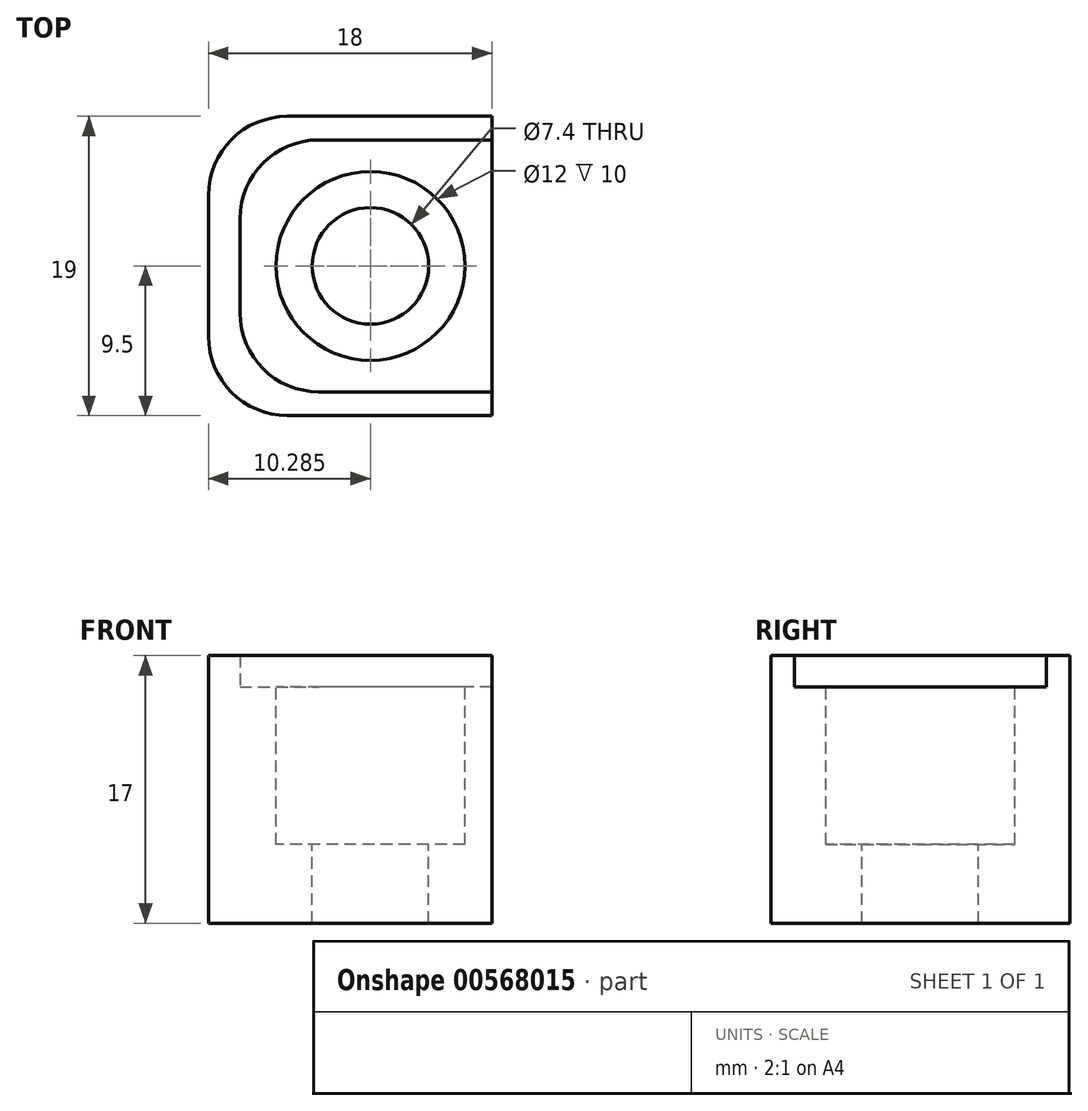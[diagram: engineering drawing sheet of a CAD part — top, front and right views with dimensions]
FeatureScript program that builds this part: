
annotation { "Feature Type Name" : "Feature", "Feature Type Description" : "" }
export const myFeature = defineFeature(function(context is Context, id is Id, definition is map)
    precondition{}
    {
        {
            var Q0;
            Q0=qCreatedBy(makeId("Top.planeOp"),FACE);
            var sketch = newSketch(context, id + "F0", { "sketchPlane" : qUnion([Q0])});
            skLineSegment(sketch, "E0.bottom", {"start": v(8, -8) * mm, "end": v(-8, -8) * mm});
            skLineSegment(sketch, "E0.top", {"start": v(8, 8) * mm, "end": v(-8, 8) * mm});
            skLineSegment(sketch, "E0.left", {"start": v(8, -8) * mm, "end": v(8, 8) * mm});
            skLineSegment(sketch, "E0.right", {"start": v(-8, -8) * mm, "end": v(-8, 8) * mm});
            skPoint(sketch, "E0.middle", {"position": v(0, 0) * mm});
            skLineSegment(sketch, "E1.bottom", {"start": v(8, -9.5) * mm, "end": v(-10, -9.5) * mm});
            skLineSegment(sketch, "E1.top", {"start": v(8, 9.5) * mm, "end": v(-10, 9.5) * mm});
            skLineSegment(sketch, "E1.right", {"start": v(-10, -9.5) * mm, "end": v(-10, 9.5) * mm});
            skLineSegment(sketch, "E2", {"start": v(8, 8) * mm, "end": v(8, 9.5) * mm});
            skLineSegment(sketch, "E3", {"start": v(8, -8) * mm, "end": v(8, -9.5) * mm});
            skPoint(sketch, "E1.left.end.orphan", {"position": v(10, 9.5) * mm});
            skPoint(sketch, "E4.orphan", {"position": v(10, -9.5) * mm});
            skCircle(sketch, "E5", {"center": v(0.29, 0) * mm, "radius": 6 * mm});
            skCircle(sketch, "E6", {"center": v(0.29, 0) * mm, "radius": 3.7 * mm});
            skSolve(sketch);
        }
        {
            var Q0;
            Q0=makeQuery(id+"F0.imprint","IMPRINT",FACE,{"disambiguationData":[TD([[makeQuery(id+"F0.imprint","IMPRINT",EDGE,{"derivedFrom":sQuery(id+"F0.wireOp",EDGE,"E0.bottom")}),-1.0]])]});
            var Q1;
            Q1=makeQuery(id+"F0.imprint","IMPRINT",FACE,{"disambiguationData":[TD([[makeQuery(id+"F0.imprint","IMPRINT",EDGE,{"derivedFrom":sQuery(id+"F0.wireOp",EDGE,"E5")}),1.0]])]});
            extrude(context, id + "F1", {"entities" : qUnion([Q0, Q1]), "oppositeDirection" : true, "depth" : 15 * mm, "offsetDistance" : 25 * mm});
        }
        {
            var Q0;
            Q0=makeQuery(id+"F0.imprint","IMPRINT",FACE,{"disambiguationData":[TD([[makeQuery(id+"F0.imprint","IMPRINT",EDGE,{"derivedFrom":sQuery(id+"F0.wireOp",EDGE,"E0.bottom")}),1.0]])]});
            extrude(context, id + "F2", {"entities" : qUnion([Q0]), "operationType" : NewBodyOperationType.ADD, "depth" : 2 * mm, "offsetDistance" : 25 * mm, "hasSecondDirection" : true, "secondDirectionOppositeDirection" : true, "secondDirectionDepth" : 15 * mm});
        }
        {
            var Q0;
            Q0=makeQuery(id+"F2.opExtrude","SWEPT_EDGE",EDGE,{"disambiguationData":[OSD([sQuery(id+"F0.wireOp",EDGE,"E0.top"),sQuery(id+"F0.wireOp",EDGE,"E0.right")])]});
            var Q1;
            Q1=makeQuery(id+"F2.opExtrude","SWEPT_EDGE",EDGE,{"disambiguationData":[OSD([sQuery(id+"F0.wireOp",EDGE,"E0.bottom"),sQuery(id+"F0.wireOp",EDGE,"E0.right")])]});
            var Q2;
            Q2=makeQuery(id+"F2.opExtrude","SWEPT_EDGE",EDGE,{"disambiguationData":[OSD([sQuery(id+"F0.wireOp",EDGE,"E1.top"),sQuery(id+"F0.wireOp",EDGE,"E1.right")])]});
            var Q3;
            Q3=makeQuery(id+"F2.opExtrude","SWEPT_EDGE",EDGE,{"disambiguationData":[OSD([sQuery(id+"F0.wireOp",EDGE,"E1.bottom"),sQuery(id+"F0.wireOp",EDGE,"E1.right")])]});
            fillet(context, id + "F3", {"entities" : qUnion([Q0, Q1, Q2, Q3]), "radius" : 5 * mm, "tangentPropagation" : true, "allowEdgeOverflow" : false});
        }
        {
            var Q0;
            Q0=makeQuery(id+"F0.imprint","IMPRINT",FACE,{"disambiguationData":[TD([[makeQuery(id+"F0.imprint","IMPRINT",EDGE,{"derivedFrom":sQuery(id+"F0.wireOp",EDGE,"E5")}),1.0]])]});
            extrude(context, id + "F4", {"entities" : qUnion([Q0]), "operationType" : NewBodyOperationType.REMOVE, "oppositeDirection" : true, "depth" : 10 * mm, "offsetDistance" : 25 * mm});
        }
    });
